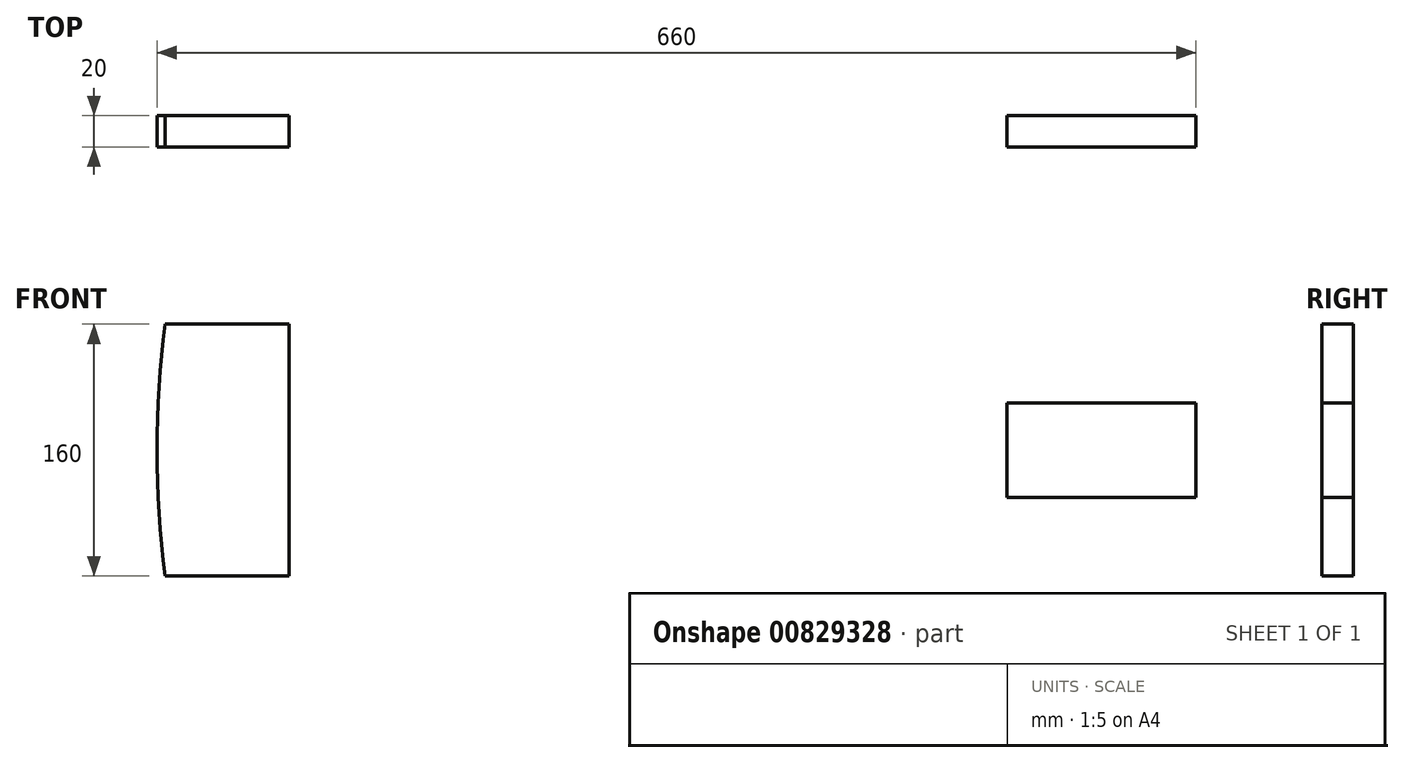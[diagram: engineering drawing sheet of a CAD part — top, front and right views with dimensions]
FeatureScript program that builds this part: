
annotation { "Feature Type Name" : "Feature", "Feature Type Description" : "" }
export const myFeature = defineFeature(function(context is Context, id is Id, definition is map)
    precondition{}
    {
        {
            var Q0;
            Q0=qCreatedBy(makeId("Front.planeOp"),FACE);
            var sketch = newSketch(context, id + "F0", { "sketchPlane" : qUnion([Q0])});
            skLineSegment(sketch, "E0.bottom", {"start": v(41.99, -80) * mm, "end": v(-36.63, -80) * mm});
            skLineSegment(sketch, "E0.top", {"start": v(41.99, 80) * mm, "end": v(-36.63, 80) * mm});
            skLineSegment(sketch, "E0.left", {"start": v(41.99, -80) * mm, "end": v(41.99, 80) * mm});
            skPoint(sketch, "E0.middle", {"position": v(0, 0) * mm});
            skLineSegment(sketch, "E1", {"start": v(-41.99, 0) * mm, "end": v(558.01, 0) * mm});
            skArc(sketch, "E2", {"start": v(-36.63, 80) * mm, "mid": v(-41.99, 0) * mm, "end": v(-36.63, -80) * mm});
            skPoint(sketch, "E3.orphan", {"position": v(-41.99, 80) * mm});
            skPoint(sketch, "E4.orphan", {"position": v(-41.99, -80) * mm});
            skLineSegment(sketch, "E5.bottom", {"start": v(498.01, -30) * mm, "end": v(618.01, -30) * mm});
            skLineSegment(sketch, "E5.top", {"start": v(498.01, 30) * mm, "end": v(618.01, 30) * mm});
            skLineSegment(sketch, "E5.left", {"start": v(498.01, -30) * mm, "end": v(498.01, 30) * mm});
            skLineSegment(sketch, "E5.right", {"start": v(618.01, -30) * mm, "end": v(618.01, 30) * mm});
            skSolve(sketch);
        }
        {
            var Q0;
            {var subQ0=sQuery(id+"F0.wireOp",EDGE,"E0.bottom");Q0=makeQuery(id+"F0.imprint","IMPRINT",FACE,{"disambiguationData":[TD([[makeQuery(id+"F0.imprint","IMPRINT",EDGE,{"derivedFrom":subQ0}),-1.0]])]});}
            var Q1;
            {var subQ0=sQuery(id+"F0.wireOp",EDGE,"E0.top");Q1=makeQuery(id+"F0.imprint","IMPRINT",FACE,{"disambiguationData":[TD([[makeQuery(id+"F0.imprint","IMPRINT",EDGE,{"derivedFrom":subQ0}),1.0]])]});}
            extrude(context, id + "F1", {"entities" : qUnion([Q0, Q1]), "depth" : 20 * mm, "offsetDistance" : 25 * mm});
        }
        {
            var Q0;
            {var subQ3=sQuery(id+"F0.wireOp",EDGE,"E5.bottom");Q0=makeQuery(id+"F0.imprint","IMPRINT",FACE,{"disambiguationData":[TD([[makeQuery(id+"F0.imprint","IMPRINT",EDGE,{"derivedFrom":subQ3}),1.0]])]});}
            extrude(context, id + "F2", {"entities" : qUnion([Q0]), "depth" : 20 * mm, "offsetDistance" : 25 * mm});
        }
    });
